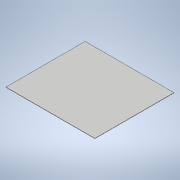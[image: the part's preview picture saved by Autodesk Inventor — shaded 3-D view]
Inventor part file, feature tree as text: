
AUTODESK INVENTOR PART (.ipt)
format: ipt  version: 2021 (Build 250183000, 183)  size: 90,112 bytes
history: native  units: in
note: dims shown in document units (in); Inventor stores cm internally (conversion verified against a paired STEP export)
features: extrude x1, sketch x1
ambient origin geometry x8: Origin, YZ Plane, XZ Plane, XY Plane, X Axis, Y Axis, Z Axis, Center Point
bodies: Solid1 (feature_tree)
feature tree (2):
  extrude  "Extrusion1"  Depth=19.6in
  sketch  "Sketch1"  dims[d0=22.0in d1=19.6in d2=0.06in d3=0.0in]
